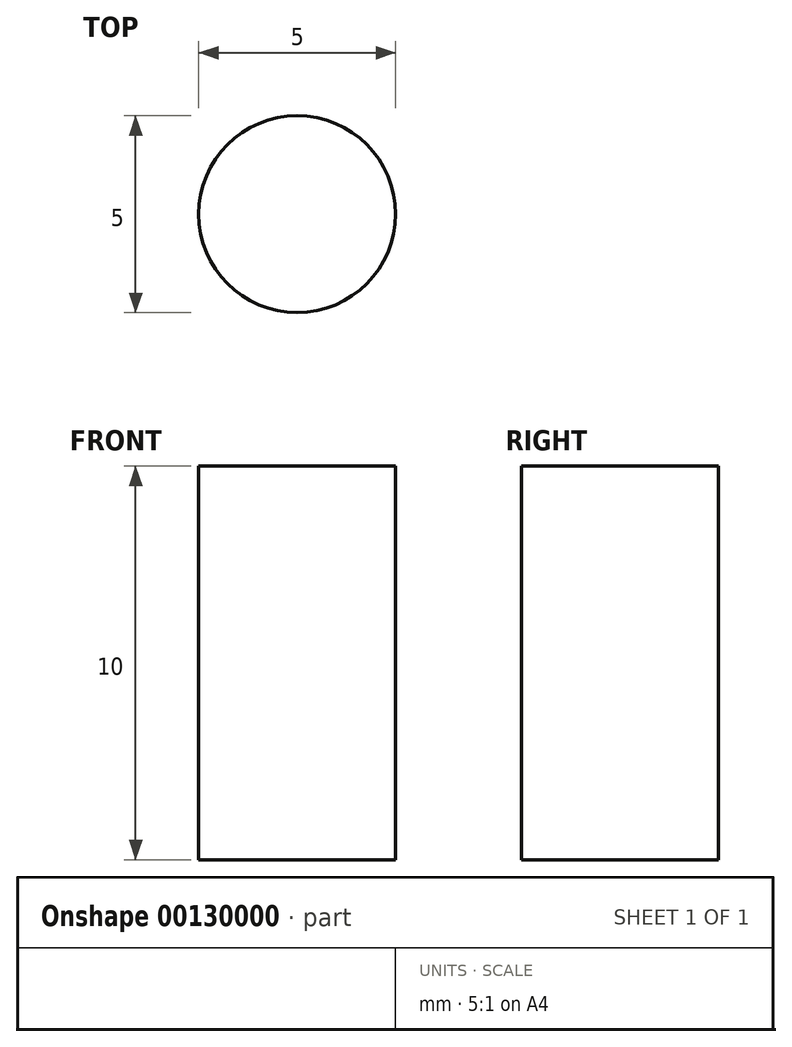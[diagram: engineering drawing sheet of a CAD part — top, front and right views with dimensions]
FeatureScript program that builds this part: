
annotation { "Feature Type Name" : "Feature", "Feature Type Description" : "" }
export const myFeature = defineFeature(function(context is Context, id is Id, definition is map)
    precondition{}
    {
        {
            var Q0;
            Q0=qCreatedBy(makeId("Top.planeOp"),FACE);
            var sketch = newSketch(context, id + "F0", { "sketchPlane" : qUnion([Q0])});
            skCircle(sketch, "E0", {"center": v(0, 0) * mm, "radius": 2.5 * mm});
            skSolve(sketch);
        }
        {
            var Q0;
            Q0 = qSketchRegion(id + "F0", true);
            extrude(context, id + "F1", {"entities" : qUnion([Q0]), "depth" : 10 * mm});
        }
    });
